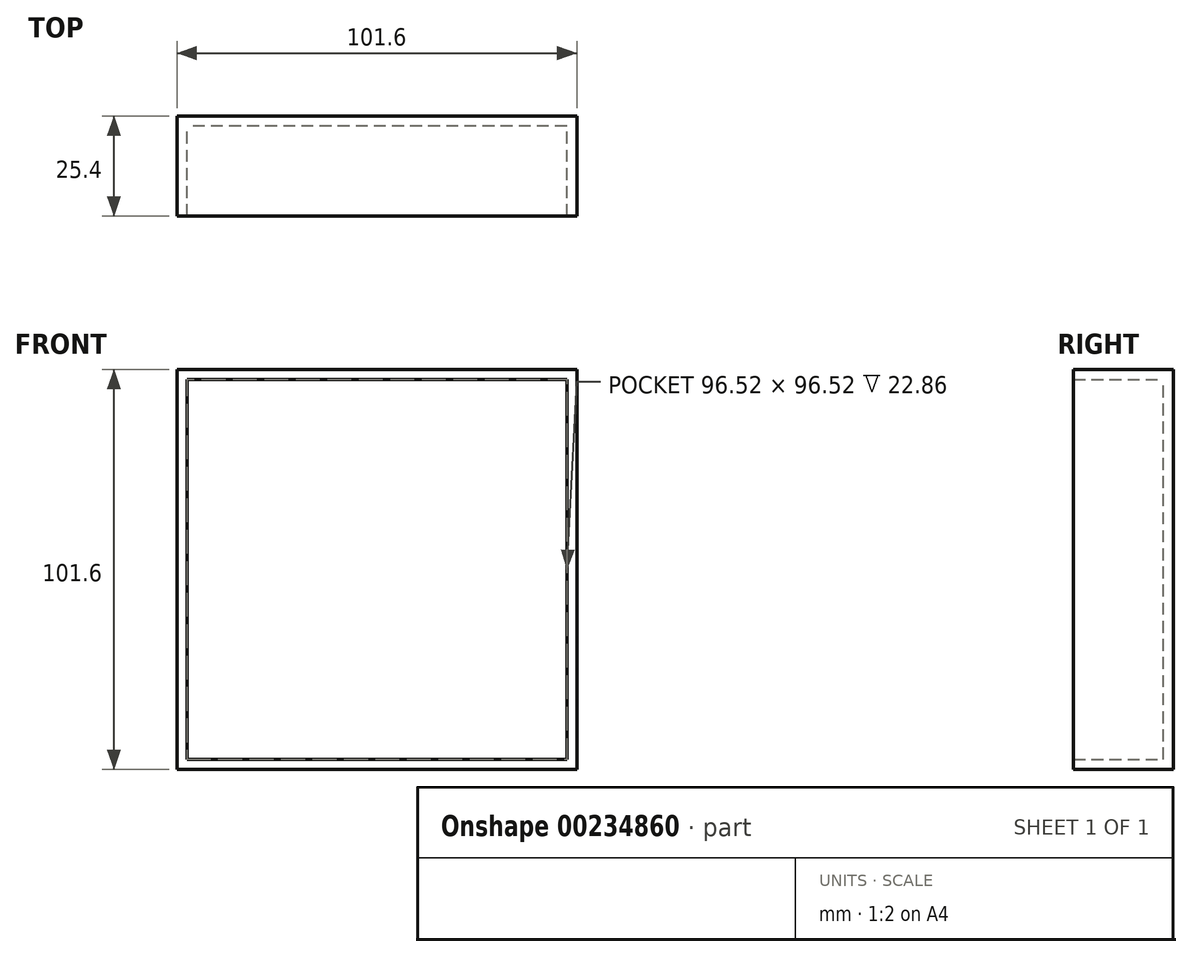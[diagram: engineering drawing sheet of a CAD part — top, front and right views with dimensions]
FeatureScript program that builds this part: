
annotation { "Feature Type Name" : "Feature", "Feature Type Description" : "" }
export const myFeature = defineFeature(function(context is Context, id is Id, definition is map)
    precondition{}
    {
        {
            var Q0;
            Q0=qCreatedBy(makeId("Front.planeOp"),FACE);
            var sketch = newSketch(context, id + "F0", { "sketchPlane" : qUnion([Q0])});
            skLineSegment(sketch, "E0.bottom", {"start": v(50.8, -50.8) * mm, "end": v(-50.8, -50.8) * mm});
            skLineSegment(sketch, "E0.top", {"start": v(50.8, 50.8) * mm, "end": v(-50.8, 50.8) * mm});
            skLineSegment(sketch, "E0.left", {"start": v(50.8, -50.8) * mm, "end": v(50.8, 50.8) * mm});
            skLineSegment(sketch, "E0.right", {"start": v(-50.8, -50.8) * mm, "end": v(-50.8, 50.8) * mm});
            skPoint(sketch, "E0.middle", {"position": v(0, 0) * mm});
            skSolve(sketch);
        }
        {
            var Q0;
            Q0 = qSketchRegion(id + "F0", true);
            var Q1;
            Q1=makeQuery(id+"F0.imprint","IMPRINT",FACE,{"disambiguationData":[TD([[makeQuery(id+"F0.imprint","IMPRINT",EDGE,{"derivedFrom":sQuery(id+"F0.wireOp",EDGE,"E0.bottom")}),-1.0]])]});
            extrude(context, id + "F1", {"entities" : qUnion([Q0, Q1]), "depth" : 25.4 * mm});
        }
        {
            var Q0;
            Q0=makeQuery(id+"F1.opExtrude","CAP_FACE",FACE,{"disambiguationData":[OSD([sQuery(id+"F0.wireOp",EDGE,"E0.bottom"),sQuery(id+"F0.wireOp",EDGE,"E0.top"),sQuery(id+"F0.wireOp",EDGE,"E0.left"),sQuery(id+"F0.wireOp",EDGE,"E0.right")])],"isStart":false});
            shell(context, id + "F3", {"entities" : qUnion([Q0]), "thickness" : 2.54 * mm});
        }
    });
